# Revit family: Gira_017730
name_source: partatom
category: Electrical Fixtures
revit_build: Autodesk Revit 2017 (Build: 20160225_1515(x64)
units: mm (PartAtom-declared; Revit-internal decimal feet)

## family parameters
Cut with Voids When Loaded = No
Host = Face
Maintain Annotation Orientation = Yes
Part Type = Normal
Room Calculation Point = No
Round Connector Dimension = Use Diameter
Shared = No

## types (1)
- Combi off/2-way SCHUKO horiz. HC WP surface-mounted grey
    Available = No
    BIM (1) = https://media.stage.bim.site
    Category = Combination switch/wall socket outlet
    Colour = White
    Data sheet (1) = https://katalog.gira.de
    Default Elevation = 1219 mm
    Description = Comb.off2w SCHUKO hori WP SM GY,Combination rocker switch SCHUKO socket outlet 16 A 250 V~ horizontal with hinged cover,Universal off 2-way switch,grey,Notes :,- Instead of the SCHUKO socket outlets, switches, buttons or light signals can also be used.,- Can also be connected with illumination.
    GTIN = 4010337177302
    HAN = 017730
    Halogen free = No
    HeinzeBIM = https://bimportal.heinze.de
    Manufacturer = Gira
    Manufacturer URL = https://www.gira.de
    Material = Other
    Material quality = Other
    Method of operation = Rocker/button
    Mounting direction = Horizontal
    Mounting method = Surface mounted (plaster)
    Name = Combi off/2-way SCHUKO horiz. HC WP surface-mounted grey
    Nominal current socket outlet = 16
    Nominal voltage = 250
    Number of socket outlets = 1
    Suitable for degree of protection (IP) = IP44
    Surface protection = Other
    Type of fastening = Mounting with screw
    Type of socket outlet = Protective contact (SCHUKO)
    Type of switch = Two-way switch
    URL = http://katalog.gira.de
    With lighting = No

## geometry (parser evidence)
native form markers: Sweep x3
no freeform markers — native parametric forms only
